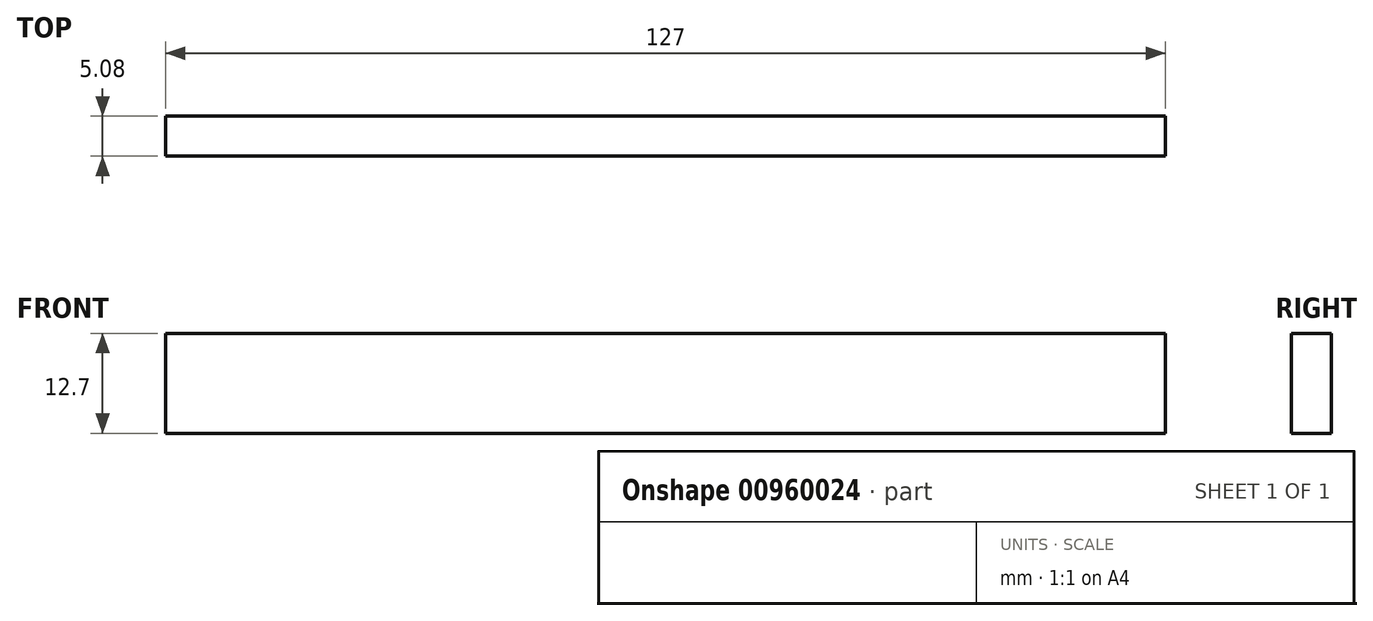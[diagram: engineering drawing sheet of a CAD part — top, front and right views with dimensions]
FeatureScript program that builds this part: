
annotation { "Feature Type Name" : "Feature", "Feature Type Description" : "" }
export const myFeature = defineFeature(function(context is Context, id is Id, definition is map)
    precondition{}
    {
        {
            var Q0;
            Q0=qCreatedBy(makeId("Front.planeOp"),FACE);
            var sketch = newSketch(context, id + "F0", { "sketchPlane" : qUnion([Q0])});
            skLineSegment(sketch, "E0.bottom", {"start": v(44.43, 0) * mm, "end": v(-82.57, 0) * mm});
            skLineSegment(sketch, "E0.top", {"start": v(44.43, 12.7) * mm, "end": v(-82.57, 12.7) * mm});
            skLineSegment(sketch, "E0.left", {"start": v(44.43, 0) * mm, "end": v(44.43, 12.7) * mm});
            skLineSegment(sketch, "E0.right", {"start": v(-82.57, 0) * mm, "end": v(-82.57, 12.7) * mm});
            skPoint(sketch, "E0.middle", {"position": v(-19.07, 6.35) * mm});
            skSolve(sketch);
        }
        {
            var Q0;
            Q0=makeQuery(id+"F0.imprint","IMPRINT",FACE,{"disambiguationData":[TD([[makeQuery(id+"F0.imprint","IMPRINT",EDGE,{"derivedFrom":sQuery(id+"F0.wireOp",EDGE,"E0.bottom")}),-1.0]])]});
            extrude(context, id + "F1", {"entities" : qUnion([Q0]), "depth" : 5.08 * mm, "offsetDistance" : 25.4 * mm});
        }
    });
